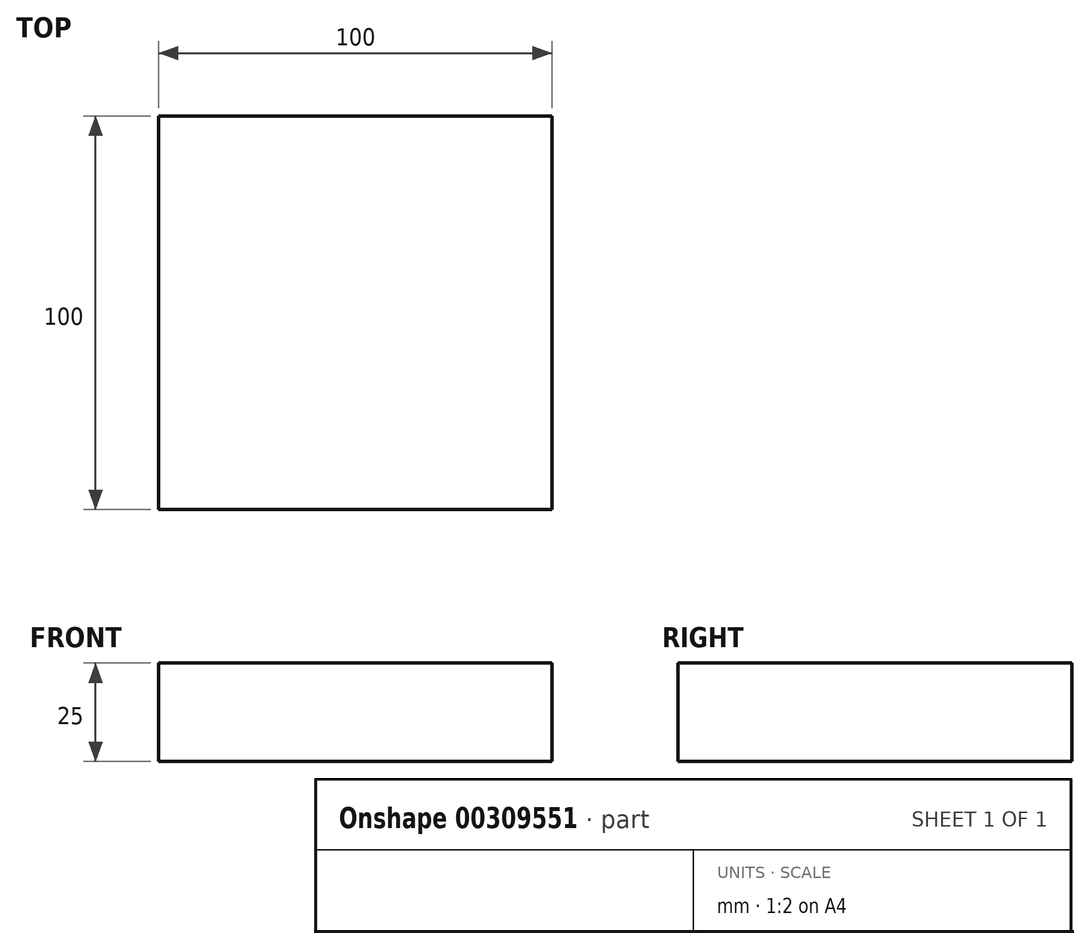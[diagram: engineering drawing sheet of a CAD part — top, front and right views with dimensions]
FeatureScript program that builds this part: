
annotation { "Feature Type Name" : "Feature", "Feature Type Description" : "" }
export const myFeature = defineFeature(function(context is Context, id is Id, definition is map)
    precondition{}
    {
        {
            var Q0;
            Q0=qCreatedBy(makeId("Front.planeOp"),FACE);
            var sketch = newSketch(context, id + "F0", { "sketchPlane" : qUnion([Q0])});
            skLineSegment(sketch, "E0.bottom", {"start": v(0, 0) * mm, "end": v(100, 0) * mm});
            skLineSegment(sketch, "E0.top", {"start": v(0, -25) * mm, "end": v(100, -25) * mm});
            skLineSegment(sketch, "E0.left", {"start": v(0, 0) * mm, "end": v(0, -25) * mm});
            skLineSegment(sketch, "E0.right", {"start": v(100, 0) * mm, "end": v(100, -25) * mm});
            skSolve(sketch);
        }
        {
            var Q0;
            Q0=makeQuery(id+"F0.imprint","IMPRINT",FACE,{"disambiguationData":[TD([[makeQuery(id+"F0.imprint","IMPRINT",EDGE,{"derivedFrom":sQuery(id+"F0.wireOp",EDGE,"E0.bottom")}),-1.0]])]});
            extrude(context, id + "F1", {"entities" : qUnion([Q0]), "oppositeDirection" : true, "depth" : 100 * mm});
        }
    });
